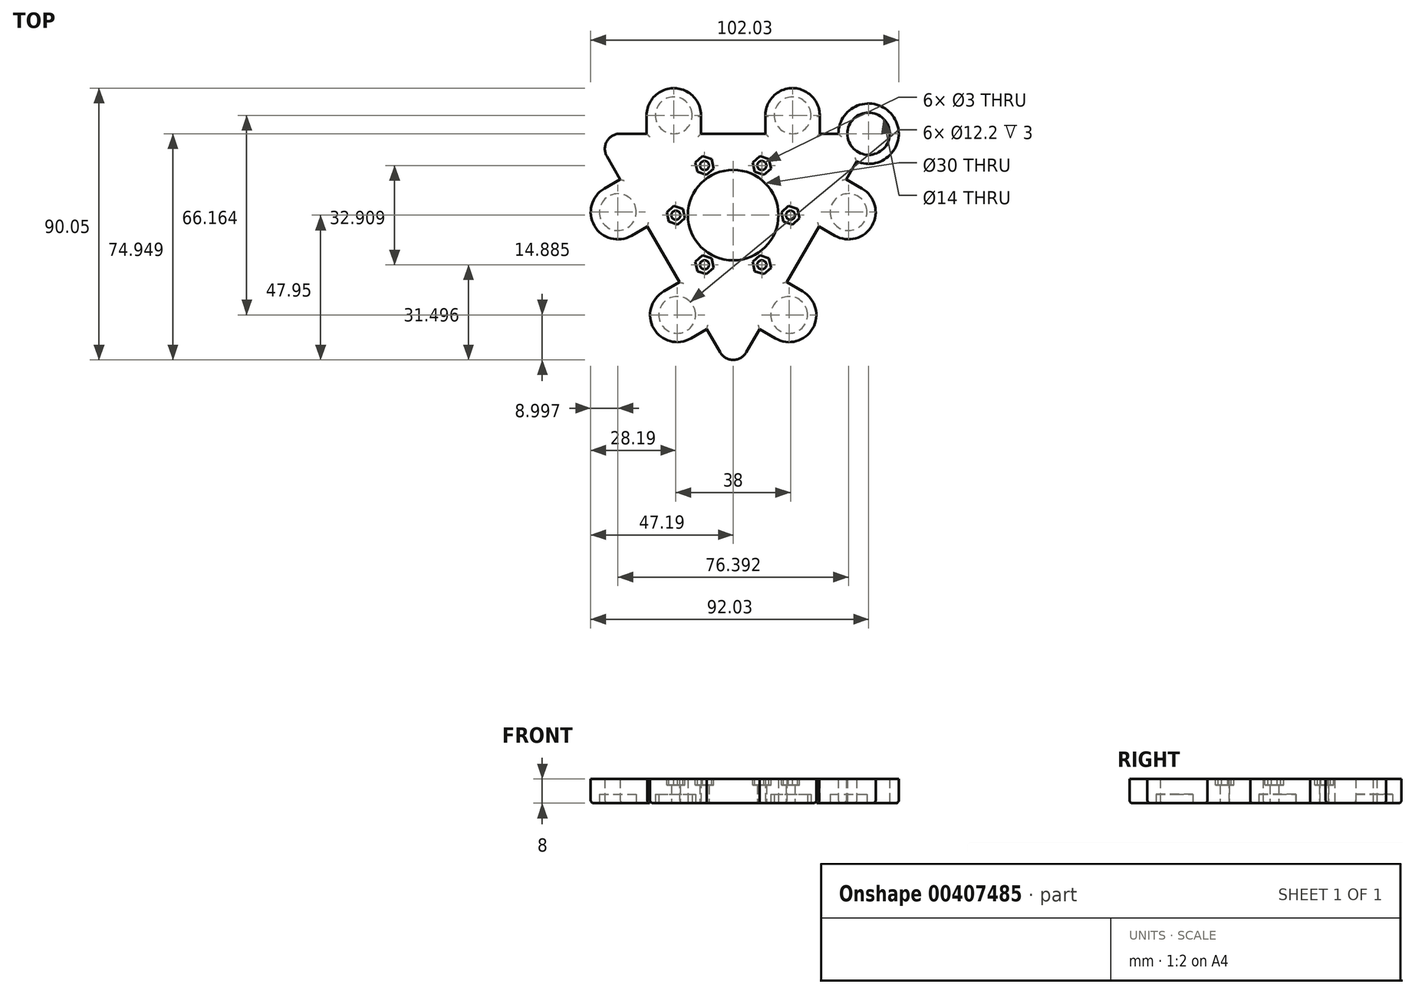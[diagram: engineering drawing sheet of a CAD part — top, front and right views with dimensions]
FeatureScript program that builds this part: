
annotation { "Feature Type Name" : "Feature", "Feature Type Description" : "" }
export const myFeature = defineFeature(function(context is Context, id is Id, definition is map)
    precondition{}
    {
        {
            var Q0;
            Q0=qCreatedBy(makeId("Top.planeOp"),FACE);
            var sketch = newSketch(context, id + "F0", { "sketchPlane" : qUnion([Q0])});
            skCircle(sketch, "E0", {"center": v(0, 0) * mm, "radius": 15 * mm});
            skCircle(sketch, "E1", {"center": v(0, 0) * mm, "radius": 21.48 * mm});
            skCircle(sketch, "E2", {"center": v(0, 0) * mm, "radius": 19 * mm});
            skCircle(sketch, "E3", {"center": v(-19, 0) * mm, "radius": 1.5 * mm});
            skCircle(sketch, "E4.1.0", {"center": v(-9.5, -16.45) * mm, "radius": 1.5 * mm});
            skCircle(sketch, "E4.2.0", {"center": v(9.5, -16.45) * mm, "radius": 1.5 * mm});
            skCircle(sketch, "E4.3.0", {"center": v(19, 0) * mm, "radius": 1.5 * mm});
            skCircle(sketch, "E4.4.0", {"center": v(9.5, 16.45) * mm, "radius": 1.5 * mm});
            skCircle(sketch, "E4.5.0", {"center": v(-9.5, 16.45) * mm, "radius": 1.5 * mm});
            skLineSegment(sketch, "E5", {"start": v(37.5, 22) * mm, "end": v(0, -42.95) * mm, "construction": true});
            skLineSegment(sketch, "E6", {"start": v(0, -42.95) * mm, "end": v(-37.5, 22) * mm, "construction": true});
            skLineSegment(sketch, "E7", {"start": v(-37.5, 22) * mm, "end": v(37.5, 22) * mm, "construction": true});
            skLineSegment(sketch, "E8.0", {"start": v(-46.16, 27) * mm, "end": v(46.16, 27) * mm});
            skLineSegment(sketch, "E8.1", {"start": v(0, -52.95) * mm, "end": v(-46.16, 27) * mm});
            skLineSegment(sketch, "E8.2", {"start": v(46.16, 27) * mm, "end": v(0, -52.95) * mm});
            skSolve(sketch);
        }
        {
            var Q0;
            Q0=makeQuery(id+"F0.imprint","IMPRINT",FACE,{"disambiguationData":[TD([[makeQuery(id+"F0.imprint","IMPRINT",EDGE,{"derivedFrom":sQuery(id+"F0.wireOp",EDGE,"E1")}),-1.0]])]});
            var Q1;
            Q1=makeQuery(id+"F0.imprint","IMPRINT",FACE,{"disambiguationData":[TD([[makeQuery(id+"F0.imprint","IMPRINT",EDGE,{"derivedFrom":sQuery(id+"F0.wireOp",EDGE,"E0")}),-1.0]])]});
            var Q2;
            Q2=makeQuery(id+"F0.imprint","IMPRINT",FACE,{"disambiguationData":[TD([[makeQuery(id+"F0.imprint","IMPRINT",EDGE,{"derivedFrom":sQuery(id+"F0.wireOp",EDGE,"E1")}),1.0]])]});
            extrude(context, id + "F1", {"entities" : qUnion([Q0, Q1, Q2]), "depth" : 8 * mm});
        }
        {
            var Q0;
            Q0=makeQuery(id+"F1.opExtrude","CAP_FACE",FACE,{"disambiguationData":[OSD([sQuery(id+"F0.wireOp",EDGE,"E0"),sQuery(id+"F0.wireOp",EDGE,"E3"),sQuery(id+"F0.wireOp",EDGE,"E4.1.0"),sQuery(id+"F0.wireOp",EDGE,"E4.2.0"),sQuery(id+"F0.wireOp",EDGE,"E4.3.0"),sQuery(id+"F0.wireOp",EDGE,"E4.4.0"),sQuery(id+"F0.wireOp",EDGE,"E4.5.0"),sQuery(id+"F0.wireOp",EDGE,"E8.0"),sQuery(id+"F0.wireOp",EDGE,"E8.1"),sQuery(id+"F0.wireOp",EDGE,"E8.2")])],"isStart":false});
            var sketch = newSketch(context, id + "F2", { "sketchPlane" : qUnion([Q0])});
            skCircle(sketch, "E9.cCircle", {"center": v(-9.5, 16.45) * mm, "radius": 2.75 * mm, "construction": true});
            skLineSegment(sketch, "E9.0", {"start": v(-6.48, 15.46) * mm, "end": v(-8.85, 13.35) * mm});
            skLineSegment(sketch, "E9.1", {"start": v(-8.85, 13.35) * mm, "end": v(-11.87, 14.34) * mm});
            skLineSegment(sketch, "E9.2", {"start": v(-11.87, 14.34) * mm, "end": v(-12.52, 17.44) * mm});
            skLineSegment(sketch, "E9.3", {"start": v(-12.52, 17.44) * mm, "end": v(-10.15, 19.56) * mm});
            skLineSegment(sketch, "E9.4", {"start": v(-10.15, 19.56) * mm, "end": v(-7.13, 18.57) * mm});
            skLineSegment(sketch, "E9.5", {"start": v(-7.13, 18.57) * mm, "end": v(-6.48, 15.46) * mm});
            skPoint(sketch, "E9.0.midPoint", {"position": v(-7.67, 14.4) * mm});
            skCircle(sketch, "E10.1.0", {"center": v(-19, 0) * mm, "radius": 2.75 * mm, "construction": true});
            skLineSegment(sketch, "E10.1.1", {"start": v(-22.02, 1) * mm, "end": v(-19.65, 3.1) * mm});
            skLineSegment(sketch, "E10.1.2", {"start": v(-19.65, 3.1) * mm, "end": v(-16.63, 2.12) * mm});
            skLineSegment(sketch, "E10.1.3", {"start": v(-16.63, 2.12) * mm, "end": v(-15.98, -1) * mm});
            skLineSegment(sketch, "E10.1.4", {"start": v(-15.98, -1) * mm, "end": v(-18.35, -3.1) * mm});
            skLineSegment(sketch, "E10.1.5", {"start": v(-18.35, -3.1) * mm, "end": v(-21.37, -2.12) * mm});
            skLineSegment(sketch, "E10.1.6", {"start": v(-21.37, -2.12) * mm, "end": v(-22.02, 1) * mm});
            skCircle(sketch, "E10.2.0", {"center": v(-9.5, -16.45) * mm, "radius": 2.75 * mm, "construction": true});
            skLineSegment(sketch, "E10.2.1", {"start": v(-11.87, -18.57) * mm, "end": v(-12.52, -15.46) * mm});
            skLineSegment(sketch, "E10.2.2", {"start": v(-12.52, -15.46) * mm, "end": v(-10.15, -13.35) * mm});
            skLineSegment(sketch, "E10.2.3", {"start": v(-10.15, -13.35) * mm, "end": v(-7.13, -14.34) * mm});
            skLineSegment(sketch, "E10.2.4", {"start": v(-7.13, -14.34) * mm, "end": v(-6.48, -17.44) * mm});
            skLineSegment(sketch, "E10.2.5", {"start": v(-6.48, -17.44) * mm, "end": v(-8.85, -19.56) * mm});
            skLineSegment(sketch, "E10.2.6", {"start": v(-8.85, -19.56) * mm, "end": v(-11.87, -18.57) * mm});
            skCircle(sketch, "E10.3.0", {"center": v(9.5, -16.45) * mm, "radius": 2.75 * mm, "construction": true});
            skLineSegment(sketch, "E10.3.1", {"start": v(10.15, -19.56) * mm, "end": v(7.13, -18.57) * mm});
            skLineSegment(sketch, "E10.3.2", {"start": v(7.13, -18.57) * mm, "end": v(6.48, -15.46) * mm});
            skLineSegment(sketch, "E10.3.3", {"start": v(6.48, -15.46) * mm, "end": v(8.85, -13.35) * mm});
            skLineSegment(sketch, "E10.3.4", {"start": v(8.85, -13.35) * mm, "end": v(11.87, -14.34) * mm});
            skLineSegment(sketch, "E10.3.5", {"start": v(11.87, -14.34) * mm, "end": v(12.52, -17.44) * mm});
            skLineSegment(sketch, "E10.3.6", {"start": v(12.52, -17.44) * mm, "end": v(10.15, -19.56) * mm});
            skCircle(sketch, "E10.4.0", {"center": v(19, 0) * mm, "radius": 2.75 * mm, "construction": true});
            skLineSegment(sketch, "E10.4.1", {"start": v(22.02, -1) * mm, "end": v(19.65, -3.1) * mm});
            skLineSegment(sketch, "E10.4.2", {"start": v(19.65, -3.1) * mm, "end": v(16.63, -2.12) * mm});
            skLineSegment(sketch, "E10.4.3", {"start": v(16.63, -2.12) * mm, "end": v(15.98, 1) * mm});
            skLineSegment(sketch, "E10.4.4", {"start": v(15.98, 1) * mm, "end": v(18.35, 3.1) * mm});
            skLineSegment(sketch, "E10.4.5", {"start": v(18.35, 3.1) * mm, "end": v(21.37, 2.12) * mm});
            skLineSegment(sketch, "E10.4.6", {"start": v(21.37, 2.12) * mm, "end": v(22.02, -1) * mm});
            skCircle(sketch, "E10.5.0", {"center": v(9.5, 16.45) * mm, "radius": 2.75 * mm, "construction": true});
            skLineSegment(sketch, "E10.5.1", {"start": v(11.87, 18.57) * mm, "end": v(12.52, 15.46) * mm});
            skLineSegment(sketch, "E10.5.2", {"start": v(12.52, 15.46) * mm, "end": v(10.15, 13.35) * mm});
            skLineSegment(sketch, "E10.5.3", {"start": v(10.15, 13.35) * mm, "end": v(7.13, 14.34) * mm});
            skLineSegment(sketch, "E10.5.4", {"start": v(7.13, 14.34) * mm, "end": v(6.48, 17.44) * mm});
            skLineSegment(sketch, "E10.5.5", {"start": v(6.48, 17.44) * mm, "end": v(8.85, 19.56) * mm});
            skLineSegment(sketch, "E10.5.6", {"start": v(8.85, 19.56) * mm, "end": v(11.87, 18.57) * mm});
            skPoint(sketch, "E10.center", {"position": v(0, 0) * mm});
            skSolve(sketch);
        }
        {
            var Q0;
            Q0=makeQuery(id+"F2.imprint","IMPRINT",FACE,{"disambiguationData":[TD([[makeQuery(id+"F2.imprint","IMPRINT",EDGE,{"derivedFrom":sQuery(id+"F2.wireOp",EDGE,"E9.0")}),-1.0]])]});
            var Q1;
            Q1=makeQuery(id+"F2.imprint","IMPRINT",FACE,{"disambiguationData":[TD([[makeQuery(id+"F2.imprint","IMPRINT",EDGE,{"derivedFrom":sQuery(id+"F2.wireOp",EDGE,"E10.5.1")}),-1.0]])]});
            var Q2;
            Q2=makeQuery(id+"F2.imprint","IMPRINT",FACE,{"disambiguationData":[TD([[makeQuery(id+"F2.imprint","IMPRINT",EDGE,{"derivedFrom":sQuery(id+"F2.wireOp",EDGE,"E10.4.1")}),-1.0]])]});
            var Q3;
            Q3=makeQuery(id+"F2.imprint","IMPRINT",FACE,{"disambiguationData":[TD([[makeQuery(id+"F2.imprint","IMPRINT",EDGE,{"derivedFrom":sQuery(id+"F2.wireOp",EDGE,"E10.3.1")}),-1.0]])]});
            var Q4;
            Q4=makeQuery(id+"F2.imprint","IMPRINT",FACE,{"disambiguationData":[TD([[makeQuery(id+"F2.imprint","IMPRINT",EDGE,{"derivedFrom":sQuery(id+"F2.wireOp",EDGE,"E10.2.1")}),-1.0]])]});
            var Q5;
            Q5=makeQuery(id+"F2.imprint","IMPRINT",FACE,{"disambiguationData":[TD([[makeQuery(id+"F2.imprint","IMPRINT",EDGE,{"derivedFrom":sQuery(id+"F2.wireOp",EDGE,"E10.1.1")}),-1.0]])]});
            extrude(context, id + "F3", {"entities" : qUnion([Q0, Q1, Q2, Q3, Q4, Q5]), "operationType" : NewBodyOperationType.REMOVE, "oppositeDirection" : true, "depth" : 2 * mm});
        }
        {
            var Q0;
            Q0=makeQuery(id+"F1.opExtrude","SWEPT_EDGE",EDGE,{"disambiguationData":[OSD([sQuery(id+"F0.wireOp",EDGE,"E8.1"),sQuery(id+"F0.wireOp",EDGE,"E8.2")])]});
            var Q1;
            Q1=makeQuery(id+"F1.opExtrude","SWEPT_EDGE",EDGE,{"disambiguationData":[OSD([sQuery(id+"F0.wireOp",EDGE,"E8.0"),sQuery(id+"F0.wireOp",EDGE,"E8.2")])]});
            var Q2;
            Q2=makeQuery(id+"F1.opExtrude","SWEPT_EDGE",EDGE,{"disambiguationData":[OSD([sQuery(id+"F0.wireOp",EDGE,"E8.0"),sQuery(id+"F0.wireOp",EDGE,"E8.1")])]});
            fillet(context, id + "F4", {"entities" : qUnion([Q0, Q1, Q2]), "radius" : 5 * mm, "tangentPropagation" : true, "allowEdgeOverflow" : false});
        }
        {
            var Q0;
            Q0=makeQuery(id+"F1.opExtrude","CAP_FACE",FACE,{"disambiguationData":[OSD([sQuery(id+"F0.wireOp",EDGE,"E0"),sQuery(id+"F0.wireOp",EDGE,"E3"),sQuery(id+"F0.wireOp",EDGE,"E4.1.0"),sQuery(id+"F0.wireOp",EDGE,"E4.2.0"),sQuery(id+"F0.wireOp",EDGE,"E4.3.0"),sQuery(id+"F0.wireOp",EDGE,"E4.4.0"),sQuery(id+"F0.wireOp",EDGE,"E4.5.0"),sQuery(id+"F0.wireOp",EDGE,"E8.0"),sQuery(id+"F0.wireOp",EDGE,"E8.1"),sQuery(id+"F0.wireOp",EDGE,"E8.2")])],"isStart":true});
            var sketch = newSketch(context, id + "F5", { "sketchPlane" : qUnion([Q0])});
            skCircle(sketch, "E11", {"center": v(-38.2, -1) * mm, "radius": 6.1 * mm});
            skCircle(sketch, "E12", {"center": v(-18.53, 33.06) * mm, "radius": 6.1 * mm});
            skCircle(sketch, "E13", {"center": v(-37.5, -22) * mm, "radius": 1.5 * mm});
            skCircle(sketch, "E14", {"center": v(0, 42.95) * mm, "radius": 1.5 * mm});
            skCircle(sketch, "E15", {"center": v(37.5, -22) * mm, "radius": 1.5 * mm});
            skCircle(sketch, "E16", {"center": v(18.53, 33.06) * mm, "radius": 6.1 * mm});
            skCircle(sketch, "E17", {"center": v(38.2, -1.01) * mm, "radius": 6.1 * mm});
            skCircle(sketch, "E18", {"center": v(-19.67, -33.1) * mm, "radius": 6.1 * mm});
            skCircle(sketch, "E19", {"center": v(19.67, -33.1) * mm, "radius": 6.1 * mm});
            skArc(sketch, "E20", {"start": v(-33.7, 6.8) * mm, "mid": v(-45.99, 3.5) * mm, "end": v(-42.7, -8.8) * mm});
            skArc(sketch, "E21", {"start": v(-14.03, 40.86) * mm, "mid": v(-26.32, 37.56) * mm, "end": v(-23.03, 25.27) * mm});
            skArc(sketch, "E22", {"start": v(23.03, 25.27) * mm, "mid": v(26.32, 37.56) * mm, "end": v(14.03, 40.86) * mm});
            skArc(sketch, "E23", {"start": v(42.7, -8.8) * mm, "mid": v(46, 3.49) * mm, "end": v(33.7, 6.78) * mm});
            skArc(sketch, "E24", {"start": v(10.68, -32.74) * mm, "mid": v(19.7, -42.1) * mm, "end": v(28.66, -32.68) * mm});
            skArc(sketch, "E25", {"start": v(-28.67, -33.1) * mm, "mid": v(-19.44, -42.1) * mm, "end": v(-10.69, -32.63) * mm});
            skLineSegment(sketch, "E26", {"start": v(-42.7, -8.8) * mm, "end": v(-37.41, -11.84) * mm});
            skLineSegment(sketch, "E27", {"start": v(-33.7, 6.8) * mm, "end": v(-28.41, 3.75) * mm});
            skLineSegment(sketch, "E28", {"start": v(-10.69, -32.63) * mm, "end": v(-10.69, -27) * mm});
            skLineSegment(sketch, "E29", {"start": v(-28.67, -33.1) * mm, "end": v(-28.67, -27) * mm});
            skLineSegment(sketch, "E30", {"start": v(10.68, -32.74) * mm, "end": v(10.68, -27) * mm});
            skLineSegment(sketch, "E31", {"start": v(28.66, -32.68) * mm, "end": v(28.66, -27) * mm});
            skLineSegment(sketch, "E32", {"start": v(33.7, 6.78) * mm, "end": v(28.42, 3.73) * mm});
            skLineSegment(sketch, "E33", {"start": v(42.7, -8.8) * mm, "end": v(37.42, -11.85) * mm});
            skLineSegment(sketch, "E34", {"start": v(23.03, 25.27) * mm, "end": v(17.74, 22.22) * mm});
            skLineSegment(sketch, "E35", {"start": v(14.03, 40.86) * mm, "end": v(8.74, 37.8) * mm});
            skLineSegment(sketch, "E36", {"start": v(-8.74, 37.8) * mm, "end": v(-14.03, 40.86) * mm});
            skLineSegment(sketch, "E37", {"start": v(-17.74, 22.22) * mm, "end": v(-23.03, 25.27) * mm});
            skLineSegment(sketch, "E38", {"start": v(-17.74, 22.22) * mm, "end": v(-8.74, 37.8) * mm});
            skLineSegment(sketch, "E39", {"start": v(8.74, 37.8) * mm, "end": v(17.74, 22.22) * mm});
            skLineSegment(sketch, "E40", {"start": v(-37.41, -11.84) * mm, "end": v(-28.41, 3.75) * mm});
            skLineSegment(sketch, "E41", {"start": v(28.42, 3.73) * mm, "end": v(37.42, -11.85) * mm});
            skLineSegment(sketch, "E42", {"start": v(28.66, -27) * mm, "end": v(10.68, -27) * mm});
            skLineSegment(sketch, "E43", {"start": v(-10.69, -27) * mm, "end": v(-28.67, -27) * mm});
            skCircle(sketch, "E44", {"center": v(44.84, -27) * mm, "radius": 7 * mm});
            skCircle(sketch, "E45", {"center": v(44.84, -27) * mm, "radius": 10 * mm});
            skSolve(sketch);
        }
        {
            var Q0;
            Q0 = qSketchRegion(id + "F5", true);
            extrude(context, id + "F6", {"entities" : qUnion([Q0]), "operationType" : NewBodyOperationType.ADD, "oppositeDirection" : true, "depth" : 8 * mm});
        }
        {
            var Q0;
            Q0=makeQuery(id+"F5.imprint","IMPRINT",FACE,{"disambiguationData":[TD([[makeQuery(id+"F5.imprint","IMPRINT",EDGE,{"derivedFrom":sQuery(id+"F5.wireOp",EDGE,"E18")}),1.0]])]});
            var Q1;
            Q1=makeQuery(id+"F5.imprint","IMPRINT",FACE,{"disambiguationData":[TD([[makeQuery(id+"F5.imprint","IMPRINT",EDGE,{"derivedFrom":sQuery(id+"F5.wireOp",EDGE,"E19")}),1.0]])]});
            var Q2;
            Q2=makeQuery(id+"F5.imprint","IMPRINT",FACE,{"disambiguationData":[TD([[makeQuery(id+"F5.imprint","IMPRINT",EDGE,{"derivedFrom":sQuery(id+"F5.wireOp",EDGE,"E17")}),1.0]])]});
            var Q3;
            Q3=makeQuery(id+"F5.imprint","IMPRINT",FACE,{"disambiguationData":[TD([[makeQuery(id+"F5.imprint","IMPRINT",EDGE,{"derivedFrom":sQuery(id+"F5.wireOp",EDGE,"E16")}),1.0]])]});
            var Q4;
            Q4=makeQuery(id+"F5.imprint","IMPRINT",FACE,{"disambiguationData":[TD([[makeQuery(id+"F5.imprint","IMPRINT",EDGE,{"derivedFrom":sQuery(id+"F5.wireOp",EDGE,"E12")}),1.0]])]});
            var Q5;
            Q5=makeQuery(id+"F5.imprint","IMPRINT",FACE,{"disambiguationData":[TD([[makeQuery(id+"F5.imprint","IMPRINT",EDGE,{"derivedFrom":sQuery(id+"F5.wireOp",EDGE,"E11")}),1.0]])]});
            extrude(context, id + "F7", {"entities" : qUnion([Q0, Q1, Q2, Q3, Q4, Q5]), "operationType" : NewBodyOperationType.REMOVE, "oppositeDirection" : true, "depth" : 3 * mm});
        }
        {
            var Q0;
            {var subQ0=sQuery(id+"F5.wireOp",EDGE,"E44");var subQ1=sQuery(id+"F0.wireOp",EDGE,"E8.2");var subQ2=sQuery(id+"F0.wireOp",EDGE,"E8.0");var subQ3=makeQuery(id+"F4.opFillet","BLEND_EDGE",EDGE,{"blendedFrom":[makeQuery(id+"F1.opExtrude","SWEPT_EDGE",EDGE,{"disambiguationData":[OSD([subQ2,subQ1])]}),makeQuery(id+"F1.opExtrude","CAP_FACE",FACE,{"disambiguationData":[OSD([sQuery(id+"F0.wireOp",EDGE,"E0"),sQuery(id+"F0.wireOp",EDGE,"E3"),sQuery(id+"F0.wireOp",EDGE,"E4.1.0"),sQuery(id+"F0.wireOp",EDGE,"E4.2.0"),sQuery(id+"F0.wireOp",EDGE,"E4.3.0"),sQuery(id+"F0.wireOp",EDGE,"E4.4.0"),sQuery(id+"F0.wireOp",EDGE,"E4.5.0"),subQ2,sQuery(id+"F0.wireOp",EDGE,"E8.1"),subQ1])],"isStart":true})],"blendedInto":[makeQuery(id+"F1.opExtrude","CAP_FACE",FACE,{"disambiguationData":[OSD([sQuery(id+"F0.wireOp",EDGE,"E0"),sQuery(id+"F0.wireOp",EDGE,"E3"),sQuery(id+"F0.wireOp",EDGE,"E4.1.0"),sQuery(id+"F0.wireOp",EDGE,"E4.2.0"),sQuery(id+"F0.wireOp",EDGE,"E4.3.0"),sQuery(id+"F0.wireOp",EDGE,"E4.4.0"),sQuery(id+"F0.wireOp",EDGE,"E4.5.0"),subQ2,sQuery(id+"F0.wireOp",EDGE,"E8.1"),subQ1])],"isStart":true})]});var subQ4=makeQuery(id+"F5.imprint","INTERSECT",VERTEX,{"disambiguationData":[OD(0.0)],"derivedFrom":[subQ3,subQ0]});Q0=makeQuery(id+"F5.imprint","IMPRINT",FACE,{"disambiguationData":[TD([[makeQuery(id+"F5.imprint","IMPRINT",EDGE,{"disambiguationData":[TD([[subQ4,1.0]])],"derivedFrom":subQ0}),1.0]])]});}
            extrude(context, id + "F8", {"entities" : qUnion([Q0]), "operationType" : NewBodyOperationType.REMOVE, "oppositeDirection" : true, "depth" : 25 * mm});
        }
        {
            var Q0;
            {var subQ0=sQuery(id+"F5.wireOp",EDGE,"E32");var subQ2=sQuery(id+"F0.wireOp",EDGE,"E8.2");Q0=makeQuery(id+"F6.boolean.opBoolean","SPLIT",EDGE,{"disambiguationData":[TD([makeQuery(id+"F6.opExtrude","SWEPT_FACE",FACE,{"disambiguationData":[OSD([subQ0])]})])],"derivedFrom":makeQuery(id+"F1.opExtrude","CAP_EDGE",EDGE,{"disambiguationData":[OSD([subQ2])],"isStart":true})});}
            var Q1;
            {var subQ0=sQuery(id+"F5.wireOp",EDGE,"E33");var subQ1=sQuery(id+"F0.wireOp",EDGE,"E8.2");Q1=makeQuery(id+"F6.boolean.opBoolean","SPLIT",EDGE,{"disambiguationData":[TD([makeQuery(id+"F6.opExtrude","SWEPT_FACE",FACE,{"disambiguationData":[OSD([subQ0])]})])],"derivedFrom":makeQuery(id+"F1.opExtrude","CAP_EDGE",EDGE,{"disambiguationData":[OSD([subQ1])],"isStart":true})});}
            var Q2;
            {var subQ0=sQuery(id+"F5.wireOp",EDGE,"E31");var subQ1=sQuery(id+"F0.wireOp",EDGE,"E8.0");Q2=makeQuery(id+"F6.boolean.opBoolean","SPLIT",EDGE,{"disambiguationData":[TD([makeQuery(id+"F6.opExtrude","SWEPT_FACE",FACE,{"disambiguationData":[OSD([subQ0])]})])],"derivedFrom":makeQuery(id+"F1.opExtrude","CAP_EDGE",EDGE,{"disambiguationData":[OSD([subQ1])],"isStart":true})});}
            var Q3;
            {var subQ0=sQuery(id+"F5.wireOp",EDGE,"E28");var subQ2=sQuery(id+"F0.wireOp",EDGE,"E8.0");Q3=makeQuery(id+"F6.boolean.opBoolean","SPLIT",EDGE,{"disambiguationData":[TD([makeQuery(id+"F6.opExtrude","SWEPT_FACE",FACE,{"disambiguationData":[OSD([subQ0])]})])],"derivedFrom":makeQuery(id+"F1.opExtrude","CAP_EDGE",EDGE,{"disambiguationData":[OSD([subQ2])],"isStart":true})});}
            var Q4;
            {var subQ0=sQuery(id+"F5.wireOp",EDGE,"E29");var subQ2=sQuery(id+"F0.wireOp",EDGE,"E8.0");Q4=makeQuery(id+"F6.boolean.opBoolean","SPLIT",EDGE,{"disambiguationData":[TD([makeQuery(id+"F6.opExtrude","SWEPT_FACE",FACE,{"disambiguationData":[OSD([subQ0])]})])],"derivedFrom":makeQuery(id+"F1.opExtrude","CAP_EDGE",EDGE,{"disambiguationData":[OSD([subQ2])],"isStart":true})});}
            var Q5;
            {var subQ0=sQuery(id+"F5.wireOp",EDGE,"E27");var subQ2=sQuery(id+"F0.wireOp",EDGE,"E8.1");Q5=makeQuery(id+"F6.boolean.opBoolean","SPLIT",EDGE,{"disambiguationData":[TD([makeQuery(id+"F6.opExtrude","SWEPT_FACE",FACE,{"disambiguationData":[OSD([subQ0])]})])],"derivedFrom":makeQuery(id+"F1.opExtrude","CAP_EDGE",EDGE,{"disambiguationData":[OSD([subQ2])],"isStart":true})});}
            var Q6;
            {var subQ0=sQuery(id+"F5.wireOp",EDGE,"E36");var subQ2=sQuery(id+"F0.wireOp",EDGE,"E8.1");Q6=makeQuery(id+"F6.boolean.opBoolean","SPLIT",EDGE,{"disambiguationData":[TD([makeQuery(id+"F6.opExtrude","SWEPT_FACE",FACE,{"disambiguationData":[OSD([subQ0])]})])],"derivedFrom":makeQuery(id+"F1.opExtrude","CAP_EDGE",EDGE,{"disambiguationData":[OSD([subQ2])],"isStart":true})});}
            var Q7;
            Q7=makeQuery(id+"F6.opExtrude","CAP_EDGE",EDGE,{"disambiguationData":[OSD([sQuery(id+"F5.wireOp",EDGE,"E20")])],"isStart":true});
            var Q8;
            Q8=makeQuery(id+"F6.opExtrude","CAP_EDGE",EDGE,{"disambiguationData":[OSD([sQuery(id+"F5.wireOp",EDGE,"E21")])],"isStart":true});
            var Q9;
            Q9=makeQuery(id+"F6.opExtrude","CAP_EDGE",EDGE,{"disambiguationData":[OSD([sQuery(id+"F5.wireOp",EDGE,"E22")])],"isStart":true});
            var Q10;
            Q10=makeQuery(id+"F6.opExtrude","CAP_EDGE",EDGE,{"disambiguationData":[OSD([sQuery(id+"F5.wireOp",EDGE,"E23")])],"isStart":true});
            var Q11;
            Q11=makeQuery(id+"F6.opExtrude","CAP_EDGE",EDGE,{"disambiguationData":[OSD([sQuery(id+"F5.wireOp",EDGE,"E24")])],"isStart":true});
            var Q12;
            Q12=makeQuery(id+"F6.opExtrude","CAP_EDGE",EDGE,{"disambiguationData":[OSD([sQuery(id+"F5.wireOp",EDGE,"E25")])],"isStart":true});
            var Q13;
            Q13=makeQuery(id+"F6.opExtrude","CAP_EDGE",EDGE,{"disambiguationData":[OSD([sQuery(id+"F5.wireOp",EDGE,"E45")])],"isStart":true});
            fillet(context, id + "F9", {"entities" : qUnion([Q0, Q1, Q2, Q3, Q4, Q5, Q6, Q7, Q8, Q9, Q10, Q11, Q12, Q13]), "radius" : 1 * mm, "tangentPropagation" : true, "allowEdgeOverflow" : false});
        }
    });
